# Revit family: Kessel 99715.80D en
name_source: partatom
category: Luftkanalzubehör
revit_build: Autodesk Revit 2017 (Build: 20160225_1515(x64)
units: mm (PartAtom-declared; Revit-internal decimal feet)

## family parameters
Arbeitsebenenbasiert = Nein
Beim Laden mit Abzugskörper schneiden = Nein
Bemaßung runder Anschluss = Durchmesser verwenden
Gemeinsam genutzt = Nein
Immer vertikal = Ja
Teiletyp = Wird verbunden mit

## types (1)
- Kessel 99715.80D en
    <CIBSE-1033.8.14> Product Literature [URL] = http://www.kessel.de
    CONNECTOR0_DIAMETER_dX_0r = 0 mm  [stored 0 ft]
    CONNECTOR0_dX_00 = 1720 mm
    CONNECTOR0_dX_01 = 1670 mm
    CONNECTOR0_ref_dX = 1670 mm
    CONNECTOR0_ref_dZ = 790 mm
    CONNECTOR1_DIAMETER_dX_0r = 0 mm  [stored 0 ft]
    CONNECTOR1_dX_00 = 1670 mm
    CONNECTOR1_dX_01 = 1720 mm
    CONNECTOR1_ref_dX = 1670 mm
    CONNECTOR1_ref_dZ = 820 mm

note: [stored X ft] marks values corroborated as IEEE doubles in the binary element streams (Revit-internal decimal feet)

## geometry (parser evidence)
native form markers: Sweep x1
no freeform markers — native parametric forms only
